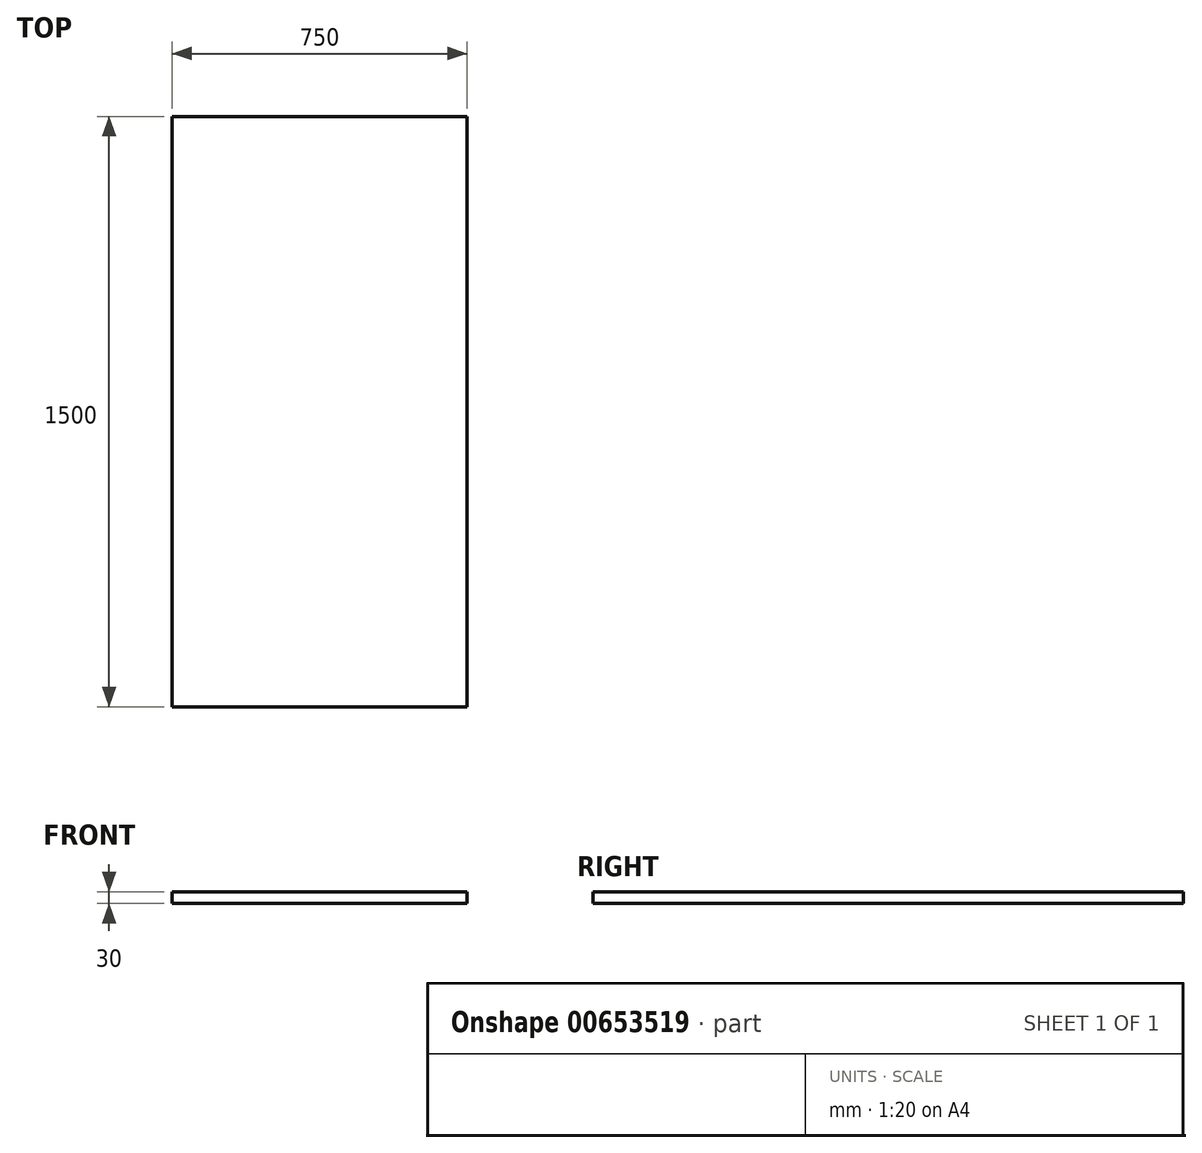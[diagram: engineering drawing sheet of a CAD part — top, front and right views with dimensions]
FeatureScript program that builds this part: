
annotation { "Feature Type Name" : "Feature", "Feature Type Description" : "" }
export const myFeature = defineFeature(function(context is Context, id is Id, definition is map)
    precondition{}
    {
        {
            var Q0;
            Q0=qCreatedBy(makeId("Top.planeOp"),FACE);
            var sketch = newSketch(context, id + "F0", { "sketchPlane" : qUnion([Q0])});
            skLineSegment(sketch, "E0.bottom", {"start": v(-25.87, -57.84) * mm, "end": v(724.13, -57.84) * mm});
            skLineSegment(sketch, "E0.top", {"start": v(-25.87, 1442.16) * mm, "end": v(724.13, 1442.16) * mm});
            skLineSegment(sketch, "E0.left", {"start": v(-25.87, -57.84) * mm, "end": v(-25.87, 1442.16) * mm});
            skLineSegment(sketch, "E0.right", {"start": v(724.13, -57.84) * mm, "end": v(724.13, 1442.16) * mm});
            skSolve(sketch);
        }
        {
            var Q0;
            Q0=makeQuery(id+"F0.imprint","IMPRINT",FACE,{"disambiguationData":[TD([[makeQuery(id+"F0.imprint","IMPRINT",EDGE,{"derivedFrom":sQuery(id+"F0.wireOp",EDGE,"E0.bottom")}),1.0]])]});
            extrude(context, id + "F1", {"entities" : qUnion([Q0]), "depth" : 30 * mm, "offsetDistance" : 25 * mm});
        }
    });
